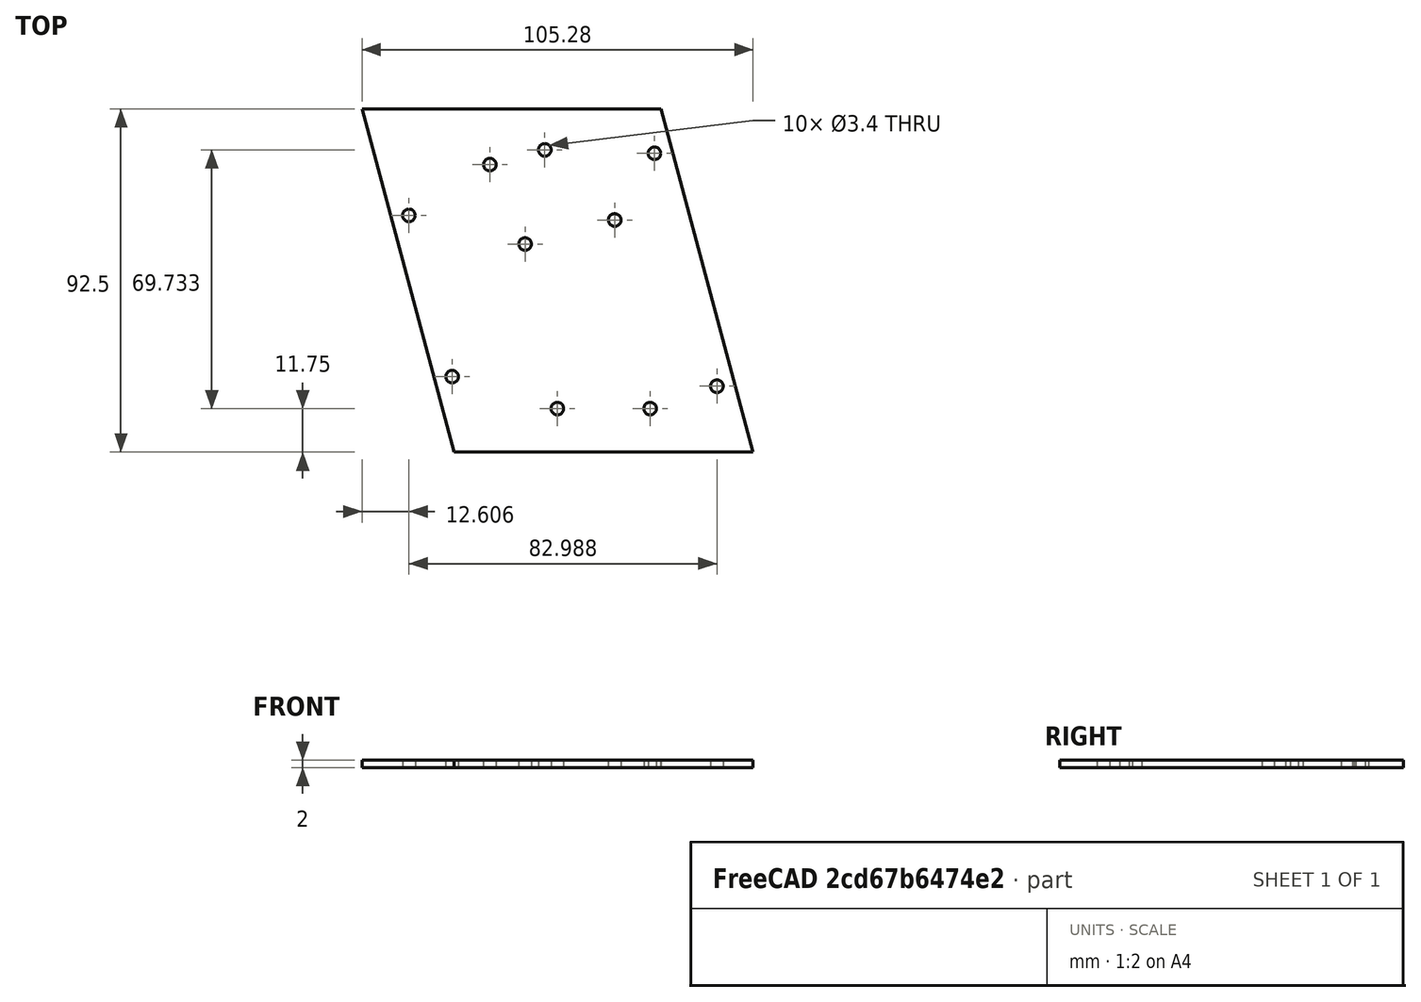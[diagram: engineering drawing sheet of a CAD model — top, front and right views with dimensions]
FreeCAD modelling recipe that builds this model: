
FCSTD DOCUMENT  (FreeCAD 0.21R33668 +26 (Git))
Label: Casing_Lid_2
License: All rights reserved
LicenseURL: https://en.wikipedia.org/wiki/All_rights_reserved
objects: Sketcher::SketchObject×3, App::DocumentObjectGroup×3, PartDesign::Hole×2, PartDesign::CoordinateSystem×2, Spreadsheet::Sheet×1, PartDesign::Pad×1, PartDesign::Body×1, App::FeaturePython×1, App::Part×1, Mesh::Feature×1
note: 12 computed .brp shape members not serialized (recipe doc carries the construction recipe); baked Part::Feature solids carry a one-line shape summary decoded from their .brp
EXTERNAL_REF file=Casing2.FCStd obj=Spreadsheet

FEATURE [Sketcher::SketchObject] Sketch
  FullyConstrained = true
  MapMode = 5
  Support = -> [XY_Plane]
  expr: Constraints[7] = 90 ° - Spreadsheet.slant
  expr: Constraints[8] = Spreadsheet.main_case_length - Spreadsheet.walls_thickness - Spreadsheet.front_thickness - Spreadsheet.clearance
  expr: Constraints[9] = Spreadsheet.main_case_height - Spreadsheet.walls_thickness * 2 - Spreadsheet.clearance
  sketch-geometry (4):
    g0: LineSegment StartX=-52.6427 StartY=46.25 StartZ=0 EndX=27.8573 EndY=46.25 EndZ=0
    g1: LineSegment StartX=27.8573 StartY=46.25 StartZ=0 EndX=52.6427 EndY=-46.25 EndZ=0
    g2: LineSegment StartX=52.6427 StartY=-46.25 StartZ=0 EndX=-27.8573 EndY=-46.25 EndZ=0
    g3: LineSegment StartX=-27.8573 StartY=-46.25 StartZ=0 EndX=-52.6427 EndY=46.25 EndZ=0
  constraints (10):
    c: Coincident(g0,g1)
    c: Coincident(g1,g2)
    c: Coincident(g2,g3)
    c: Coincident(g3,g0)
    c: Horizontal(g0)
    c: Symmetric(g0,g1,g-1)
    c: Symmetric(g0,g2,g-1)
    c: Angle(g1,g2) = 1.309
    c: DistanceY(g3,g3) = 92.5
    c: DistanceX(g0,g0) = 80.5
FEATURE [Spreadsheet::Sheet] Spreadsheet
  cells = B2='slant; C2(slant)==<<Casing2>>#Spreadsheet.slant; E2='main_case_width; F2(main_case_width)==<<Casing2>>#Spreadsheet.main_case_width; H2='display_width; I2(display_width)==<<Casing2>>#Spreadsheet.display_width; B3='walls_thickness; C3(walls_thickness)==<<Casing2>>#Spreadsheet.walls_thickness; E3='main_case_height; F3(main_case_height)==<<Casing2>>#Spreadsheet.main_case_height; H3='display_height; I3(display_height)==<<Casing2>>#Spreadsheet.display_height; B4='screw_radius; C4(screw_radius)==<<Casing2>>#Spreadsheet.screw_radius; E4='main_case_length; F4(main_case_length)==<<Casing2>>#Spreadsheet.main_case_length; B5='front_thickness; C5(front_thickness)==<<Casing2>>#Spreadsheet.front_thickness; H5='mlx_cam_height; I5(mlx_cam_height)==<<Casing2>>#Spreadsheet.mlx_cam_height; B6='clearance; C6(clearance)==0.5 mm; E6='mlx_carrier_height; F6(mlx_carrier_height)==<<Casing2>>#Spreadsheet.mlx_carrier_height; H6='mlx_extra_space; I6(mlx_extra_space)==<<Casing2>>#Spreadsheet.mlx_extra_space; E7='mlx_carrier_width; F7(mlx_carrier_width)==<<Casing2>>#Spreadsheet.mlx_carrier_width; H7='mlx_radius; I7(mlx_radius)==<<Casing2>>#Spreadsheet.mlx_extra_space; B9='display_guard_depth; C9(display_guard_depth)==<<Casing2>>#Spreadsheet.display_guard_depth; E9='beams_width; F9(beams_width)==<<Casing2>>#Spreadsheet.beams_width; H9='raspi_carrier_hole_dist; I9(raspi_carrier_hole_dist)==<<Casing2>>#Spreadsheet.raspi_carrier_hole_dist; B10='display_guard_size; C10(display_guard_size)==<<Casing2>>#Spreadsheet.display_guard_size; E10='beams_height; F10(beams_height)==<<Casing2>>#Spreadsheet.beams_height; H10='raspi_carrier_height; I10(raspi_carrier_height)==<<Casing2>>#Spreadsheet.raspi_carrier_height; B11='display_clearance; C11(display_clearance)==<<Casing2>>#Spreadsheet.display_clearance; H11='raspi_carrier_depth; I11(raspi_carrier_depth)==<<Casing2>>#Spreadsheet.raspi_carrier_depth; B12='display_hole_depth; C12(display_hole_depth)==<<Casing2>>#Spreadsheet.display_hole_depth; E12='beam_LB_offset; F12(beam_LB_offset)==<<Casing2>>#Spreadsheet.beam_LB_offset; E13='beam_LF_offset; F13(beam_LF_offset)==<<Casing2>>#Spreadsheet.beam_LF_offset; B14='display_thickness; C14(display_thickness)==<<Casing2>>#Spreadsheet.display_thickness; E14='beam_UB_offset; F14(beam_UB_offset)==<<Casing2>>#Spreadsheet.beam_UB_offset; B15='display_carrier_height; C15(display_carrier_height)==<<Casing2>>#Spreadsheet.display_carrier_height; E15='beam_UF_offset; F15(beam_UF_offset)==<<Casing2>>#Spreadsheet.beam_UF_offset; B17='display_carrier_hole_dist; C17(display_carrier_hole_dist)==<<Casing2>>#Spreadsheet.display_carrier_hole_dist; B18='display_carrier_offset; C18(display_carrier_offset)==<<Casing2>>#Spreadsheet.display_carrier_offset
FEATURE [PartDesign::Pad] Pad
  Direction = (0,0,1)
  Length = 2
  Length2 = 10
  Profile = -> Sketch
  ReferenceAxis = -> Sketch [N_Axis]
  Type = 0
  expr: Length = Spreadsheet.walls_thickness
FEATURE [Sketcher::SketchObject] Sketch001
  FullyConstrained = true
  MapMode = 5
  Placement = pos=(0,0,2) rot=(0,0,1;0rad)
  Support = -> [Pad]
  expr: Constraints[25] = Spreadsheet.mlx_cam_height + Spreadsheet.front_thickness + Spreadsheet.mlx_extra_space
  expr: Constraints[26] = Spreadsheet.display_carrier_offset
  expr: Constraints[27] = Spreadsheet.display_carrier_hole_dist
  expr: Constraints[28] = Spreadsheet.walls_thickness
  expr: Constraints[29] = Spreadsheet.raspi_carrier_height
  expr: Constraints[30] = Spreadsheet.raspi_carrier_hole_dist
  expr: Constraints[32] = Spreadsheet.screw_radius
  expr: Constraints[33] = Spreadsheet.screw_radius
  expr: Constraints[34] = Spreadsheet.screw_radius
  expr: Constraints[35] = Spreadsheet.screw_radius
  expr: Constraints[36] = Spreadsheet.screw_radius
  expr: Constraints[37] = Spreadsheet.screw_radius
  expr: Constraints[40] = Spreadsheet.front_thickness
  expr: Constraints[43] = Spreadsheet.walls_thickness / cos(Spreadsheet.slant)
  expr: Constraints[47] = Spreadsheet.walls_thickness / cos(Spreadsheet.slant)
  expr: Constraints[59] = Spreadsheet.mlx_carrier_height - Spreadsheet.mlx_carrier_width
  expr: Constraints[5] = 90 ° - Spreadsheet.slant
  expr: Constraints[60] = 90 ° - Spreadsheet.slant
  expr: Constraints[8] = Spreadsheet.main_case_length - Spreadsheet.walls_thickness - Spreadsheet.front_thickness
  expr: Constraints[9] = Spreadsheet.main_case_height - Spreadsheet.walls_thickness * 2
  sketch-geometry (24):
    g0: LineSegment StartX=-52.9596 StartY=46.5 StartZ=0 EndX=28.0404 EndY=46.5 EndZ=0
    g1: LineSegment StartX=28.0404 StartY=46.5 StartZ=0 EndX=52.9596 EndY=-46.5 EndZ=0
    g2: LineSegment StartX=52.9596 StartY=-46.5 StartZ=0 EndX=-28.0404 EndY=-46.5 EndZ=0
    g3: LineSegment StartX=-28.0404 StartY=-46.5 StartZ=0 EndX=-52.9596 EndY=46.5 EndZ=0
    g4: LineSegment StartX=-15.7177 StartY=51.5 StartZ=0 EndX=-10.8276 EndY=33.25 EndZ=0
    g5: LineSegment StartX=-18.2266 StartY=31.2674 StartZ=0 EndX=-3.42864 EndY=35.2326 EndZ=0
    g6: LineSegment StartX=12.4596 StartY=-46.5 StartZ=0 EndX=12.4596 EndY=-34.5 EndZ=0
    g7: LineSegment StartX=-0.0403626 StartY=-34.5 StartZ=0 EndX=24.9596 EndY=-34.5 EndZ=0
    g8: LineSegment StartX=34.7391 StartY=21.5 StartZ=0 EndX=-26.1142 EndY=5.1944 EndZ=0
    g9: GeomPoint X=32.8072 Y=20.9824 Z=0
    g10: GeomPoint X=3.3465 Y=13.0884 Z=0
    g11: Circle CenterX=-3.42864 CenterY=35.2326 CenterZ=0 NormalX=0 NormalY=0 NormalZ=1 AngleXU=0 Radius=1.5
    g12: Circle CenterX=-18.2266 CenterY=31.2674 CenterZ=0 NormalX=0 NormalY=0 NormalZ=1 AngleXU=0 Radius=1.5
    g13: Circle CenterX=15.4206 CenterY=16.3236 CenterZ=0 NormalX=0 NormalY=0 NormalZ=1 AngleXU=0 Radius=1.5
    g14: Circle CenterX=-8.72757 CenterY=9.85314 CenterZ=0 NormalX=0 NormalY=0 NormalZ=1 AngleXU=0 Radius=1.5
    g15: Circle CenterX=24.9596 CenterY=-34.5 CenterZ=0 NormalX=0 NormalY=0 NormalZ=1 AngleXU=0 Radius=1.5
    g16: Circle CenterX=-0.0403626 CenterY=-34.5 CenterZ=0 NormalX=0 NormalY=0 NormalZ=1 AngleXU=0 Radius=1.5
    g17: LineSegment StartX=-52.9596 StartY=46.5 StartZ=0 EndX=-54.2994 EndY=51.5 EndZ=0
    g18: LineSegment StartX=-56.3699 StartY=51.5 StartZ=0 EndX=28.7712 EndY=51.5 EndZ=0
    g19: LineSegment StartX=28.0404 StartY=46.5 StartZ=0 EndX=26.7006 EndY=51.5 EndZ=0
    g20: ArcOfCircle CenterX=24.9345 CenterY=46.5 CenterZ=0 NormalX=0 NormalY=0 NormalZ=1 AngleXU=0 Radius=5 StartAngle=0.261799 EndAngle=1.5708
    g21: LineSegment StartX=28.7712 StartY=51.5 StartZ=0 EndX=29.7642 EndY=47.7941 EndZ=0
    g22: LineSegment StartX=24.9345 StartY=51.5 StartZ=0 EndX=28.7712 EndY=51.5 EndZ=0
    g23: GeomPoint X=-15.7177 Y=51.5 Z=0
  constraints (61):
    c: Coincident(g0,g1)
    c: Coincident(g1,g2)
    c: Coincident(g2,g3)
    c: Coincident(g3,g0)
    c: Horizontal(g0)
    c: Angle(g1,g2) = 1.309
    c: Symmetric(g0,g1,g-1)
    c: Symmetric(g0,g2,g-1)
    c: DistanceY(g3,g3) = 93
    c: DistanceX(g0,g0) = 81
    c: Vertical(g6)
    c: Horizontal(g7)
    c: Symmetric(g5,g5,g4)
    c: Symmetric(g1,g2,g6)
    c: Symmetric(g7,g7,g6)
    c: PointOnObject(g8,g1)
    c: PointOnObject(g9,g8)
    c: Symmetric(g9,g8,g10)
    c: Coincident(g11,g5)
    c: Coincident(g12,g5)
    c: PointOnObject(g14,g8)
    c: Coincident(g15,g7)
    c: Coincident(g16,g7)
    c: Symmetric(g13,g14,g10)
    c: Perpendicular(g8,g1)
    c: DistanceY(g4,g4) = 18.25
    c: DistanceY(g6,g6) = 12
    c: DistanceX(g7,g7) = 25
    c: Distance(g9,g8) = 2
    c: Distance(g9,g8) = 61
    c: Distance(g13,g14) = 25
    c: DistanceY(g8,g0) = 25
    c: Radius(g12) = 1.5
    c: Radius(g11) = 1.5
    c: Radius(g14) = 1.5
    c: Radius(g13) = 1.5
    c: Radius(g16) = 1.5
    c: Radius(g15) = 1.5
    c: Coincident(g17,g0)
    c: Parallel(g3,g17)
    c: DistanceY(g0,g17) = 5
    c: Horizontal(g18)
    c: PointOnObject(g17,g18)
    c: DistanceX(g18,g17) = 2.07055
    c: Coincident(g19,g0)
    c: PointOnObject(g19,g18)
    c: Parallel(g19,g1)
    c: DistanceX(g19,g18) = 2.07055
    c: Radius(g20) = 5
    c: PointOnObject(g20,g18)
    c: Coincident(g21,g18)
    c: Parallel(g21,g19)
    c: Coincident(g22,g20)
    c: Coincident(g22,g18)
    c: Equal(g22,g21)
    c: Tangent(g20,g21) = 1.5708
    c: Symmetric(g18,g20,g23)
    c: Coincident(g4,g23)
    c: Perpendicular(g5,g4)
    c: Distance(g5) = 15.32
    c: Angle(g4,g18) = 1.309
FEATURE [PartDesign::Hole] Hole
  BaseFeature = -> Pad
  CustomThreadClearance = 0
  Depth = 281.498
  DepthType = 1
  Diameter = 3.4
  DrillForDepth = false
  DrillPoint = 1
  DrillPointAngle = 118
  HoleCutCountersinkAngle = 90
  HoleCutCustomValues = false
  HoleCutDepth = 0
  HoleCutDiameter = 6.1
  HoleCutType = 0
  ModelThread = false
  Profile = -> Sketch001
  Tapered = false
  TaperedAngle = 90
  ThreadClass = 0
  ThreadDepth = 281.498
  ThreadDepthType = 0
  ThreadDirection = 0
  ThreadFit = 0
  ThreadSize = 9
  ThreadType = 1
  Threaded = false
  UseCustomThreadClearance = false
FEATURE [Sketcher::SketchObject] Sketch002
  FullyConstrained = true
  MapMode = 5
  Placement = pos=(0,0,2) rot=(0,0,1;0rad)
  Support = -> [Hole]
  expr: Constraints[46] = Spreadsheet.beams_height
  expr: Constraints[47] = Spreadsheet.beams_height
  expr: Constraints[48] = Spreadsheet.beams_height
  expr: Constraints[49] = Spreadsheet.beams_height
  expr: Constraints[50] = Spreadsheet.beams_width
  expr: Constraints[51] = Spreadsheet.beams_width
  expr: Constraints[52] = Spreadsheet.beams_width
  expr: Constraints[53] = Spreadsheet.beams_width
  expr: Constraints[58] = Spreadsheet.screw_radius
  expr: Constraints[59] = Spreadsheet.screw_radius
  expr: Constraints[60] = Spreadsheet.screw_radius
  expr: Constraints[61] = Spreadsheet.screw_radius
  expr: Constraints[62] = Spreadsheet.beam_UF_offset
  expr: Constraints[63] = Spreadsheet.beam_UB_offset
  expr: Constraints[64] = Spreadsheet.beam_LF_offset
  expr: Constraints[65] = Spreadsheet.beam_LB_offset
  expr: Constraints[7] = 90 ° - Spreadsheet.slant
  expr: Constraints[8] = Spreadsheet.main_case_length - Spreadsheet.walls_thickness - Spreadsheet.front_thickness
  expr: Constraints[9] = Spreadsheet.main_case_height - Spreadsheet.walls_thickness * 2
  sketch-geometry (24):
    g0: LineSegment StartX=-52.9596 StartY=46.5 StartZ=0 EndX=28.0404 EndY=46.5 EndZ=0
    g1: LineSegment StartX=28.0404 StartY=46.5 StartZ=0 EndX=52.9596 EndY=-46.5 EndZ=0
    g2: LineSegment StartX=52.9596 StartY=-46.5 StartZ=0 EndX=-28.0404 EndY=-46.5 EndZ=0
    g3: LineSegment StartX=-28.0404 StartY=-46.5 StartZ=0 EndX=-52.9596 EndY=46.5 EndZ=0
    g4: Circle CenterX=-40.034 CenterY=17.5793 CenterZ=0 NormalX=0 NormalY=0 NormalZ=1 AngleXU=0 Radius=1.5
    g5: Circle CenterX=-28.3871 CenterY=-25.8874 CenterZ=0 NormalX=0 NormalY=0 NormalZ=1 AngleXU=0 Radius=1.5
    g6: Circle CenterX=42.9536 CenterY=-28.4756 CenterZ=0 NormalX=0 NormalY=0 NormalZ=1 AngleXU=0 Radius=1.5
    g7: Circle CenterX=26.1304 CenterY=34.3096 CenterZ=0 NormalX=0 NormalY=0 NormalZ=1 AngleXU=0 Radius=1.5
    g8: LineSegment StartX=-46.1577 StartY=21.1148 StartZ=0 EndX=-36.4984 EndY=23.703 EndZ=0
    g9: LineSegment StartX=-36.4984 StartY=23.703 StartZ=0 EndX=-33.9102 EndY=14.0437 EndZ=0
    g10: LineSegment StartX=-33.9102 StartY=14.0437 StartZ=0 EndX=-43.5695 EndY=11.4555 EndZ=0
    g11: LineSegment StartX=-43.5695 StartY=11.4555 StartZ=0 EndX=-46.1577 EndY=21.1148 EndZ=0
    g12: LineSegment StartX=-34.5108 StartY=-22.3519 StartZ=0 EndX=-24.8516 EndY=-19.7637 EndZ=0
    g13: LineSegment StartX=-24.8516 StartY=-19.7637 StartZ=0 EndX=-22.2634 EndY=-29.4229 EndZ=0
    g14: LineSegment StartX=-22.2634 StartY=-29.4229 StartZ=0 EndX=-31.9226 EndY=-32.0111 EndZ=0
    g15: LineSegment StartX=-31.9226 StartY=-32.0111 StartZ=0 EndX=-34.5108 EndY=-22.3519 EndZ=0
    g16: LineSegment StartX=36.8299 StartY=-24.94 StartZ=0 EndX=46.4892 EndY=-22.3519 EndZ=0
    g17: LineSegment StartX=46.4892 StartY=-22.3519 StartZ=0 EndX=49.0774 EndY=-32.0111 EndZ=0
    g18: LineSegment StartX=49.0774 StartY=-32.0111 StartZ=0 EndX=39.4181 EndY=-34.5993 EndZ=0
    g19: LineSegment StartX=39.4181 StartY=-34.5993 StartZ=0 EndX=36.8299 EndY=-24.94 EndZ=0
    g20: LineSegment StartX=20.0067 StartY=37.8451 StartZ=0 EndX=29.6659 EndY=40.4333 EndZ=0
    g21: LineSegment StartX=29.6659 StartY=40.4333 StartZ=0 EndX=32.2541 EndY=30.7741 EndZ=0
    g22: LineSegment StartX=32.2541 StartY=30.7741 StartZ=0 EndX=22.5949 EndY=28.1859 EndZ=0
    g23: LineSegment StartX=22.5949 StartY=28.1859 StartZ=0 EndX=20.0067 EndY=37.8451 EndZ=0
  constraints (66):
    c: Coincident(g0,g1)
    c: Coincident(g1,g2)
    c: Coincident(g2,g3)
    c: Coincident(g3,g0)
    c: Horizontal(g0)
    c: Symmetric(g0,g2,g-1)
    c: Symmetric(g0,g1,g-1)
    c: Angle(g1,g2) = 1.309
    c: DistanceY(g3,g3) = 93
    c: DistanceX(g0,g0) = 81
    c: Coincident(g8,g9)
    c: Coincident(g9,g10)
    c: Coincident(g10,g11)
    c: Coincident(g11,g8)
    c: Coincident(g12,g13)
    c: Coincident(g13,g14)
    c: Coincident(g14,g15)
    c: Coincident(g15,g12)
    c: Coincident(g16,g17)
    c: Coincident(g17,g18)
    c: Coincident(g18,g19)
    c: Coincident(g19,g16)
    c: Coincident(g20,g21)
    c: Coincident(g21,g22)
    c: Coincident(g22,g23)
    c: Coincident(g23,g20)
    c: PointOnObject(g8,g3)
    c: PointOnObject(g10,g3)
    c: PointOnObject(g12,g3)
    c: PointOnObject(g14,g3)
    c: PointOnObject(g16,g1)
    c: PointOnObject(g17,g1)
    c: PointOnObject(g20,g1)
    c: PointOnObject(g21,g1)
    c: Equal(g11,g9)
    c: Equal(g15,g13)
    c: Equal(g17,g19)
    c: Equal(g21,g23)
    c: Parallel(g3,g9)
    c: Parallel(g3,g13)
    c: Parallel(g1,g19)
    c: Parallel(g1,g23)
    c: Perpendicular(g8,g3)
    c: Perpendicular(g12,g3)
    c: Perpendicular(g20,g1)
    c: Perpendicular(g16,g1)
    c: Distance(g8) = 10
    c: Distance(g12) = 10
    c: Distance(g16) = 10
    c: Distance(g20) = 10
    c: Distance(g9) = 10
    c: Distance(g13) = 10
    c: Distance(g23) = 10
    c: Distance(g19) = 10
    c: Symmetric(g8,g9,g4)
    c: Symmetric(g12,g13,g5)
    c: Symmetric(g20,g21,g7)
    c: Symmetric(g16,g17,g6)
    c: Radius(g4) = 1.5
    c: Radius(g5) = 1.5
    c: Radius(g7) = 1.5
    c: Radius(g6) = 1.5
    c: Distance(g14,g2) = 15
    c: Distance(g10,g2) = 60
    c: Distance(g1,g17) = 15
    c: Distance(g21,g1) = 80
FEATURE [PartDesign::Hole] Hole001
  BaseFeature = -> Hole
  CustomThreadClearance = 0
  Depth = 25
  DepthType = 0
  Diameter = 3.4
  DrillForDepth = false
  DrillPoint = 1
  DrillPointAngle = 118
  HoleCutCountersinkAngle = 90
  HoleCutCustomValues = false
  HoleCutDepth = 0
  HoleCutDiameter = 6.1
  HoleCutType = 0
  ModelThread = false
  Profile = -> Sketch002
  Tapered = false
  TaperedAngle = 90
  ThreadClass = 0
  ThreadDepth = 25
  ThreadDepthType = 0
  ThreadDirection = 0
  ThreadFit = 0
  ThreadSize = 9
  ThreadType = 1
  Threaded = false
  UseCustomThreadClearance = false
FEATURE [PartDesign::Body] Body  label="Körper"
  Group = -> [Sketch,Pad,Sketch001,Hole,Sketch002,Hole001]
  Origin = -> Origin
  Tip = -> Hole001
FEATURE [App::DocumentObjectGroup] Parts
FEATURE [PartDesign::CoordinateSystem] LCS_Origin
  AttacherType = Attacher::AttachEngine3D
  MapMode = 2
  Support = -> [X_Axis001]
FEATURE [App::DocumentObjectGroup] Constraints
FEATURE [App::FeaturePython] Variables  # WARN: FeaturePython — macro-defined, semantics opaque (R4)
  Type = App::PropertyContainer
FEATURE [App::DocumentObjectGroup] Configurations
FEATURE [PartDesign::CoordinateSystem] LCS_screw
  AttacherType = Attacher::AttachEngine3D
  MapMode = 11
  Placement = pos=(26.1304,34.3096,2) rot=(0,0,1;1.5708rad)
  Support = -> [Hole001]
FEATURE [App::Part] Model
  AssemblyType = Part::Link
  Group = -> [LCS_Origin,Constraints,Variables,Configurations,Body,LCS_screw]
  Origin = -> Origin001
  Type = Assembly
FEATURE [Mesh::Feature] Mesh  label="Körper (Meshed)"
